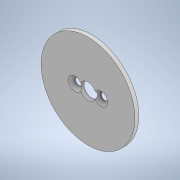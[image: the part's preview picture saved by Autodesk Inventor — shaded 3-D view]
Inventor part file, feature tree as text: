
AUTODESK INVENTOR PART (.ipt)
format: ipt  version: 2022 (Build 260153000, 153)  size: 116,736 bytes
history: native  units: mm
features: extrude x2, sketch x2, other x1, chamfer x1
ambient origin geometry x8: Origin, YZ Plane, XZ Plane, XY Plane, X Axis, Y Axis, Z Axis, Center Point
bodies: Body1 (feature_tree)
feature tree (6):
  other  "ソリッド1"
  extrude  "押し出し1"  Depth=47.0mm
  extrude  "押し出し2"  Depth=8.0mm
  chamfer  "面取り1"  Distance=2.0mm
  sketch  "スケッチ1"
  sketch  "スケッチ2"
